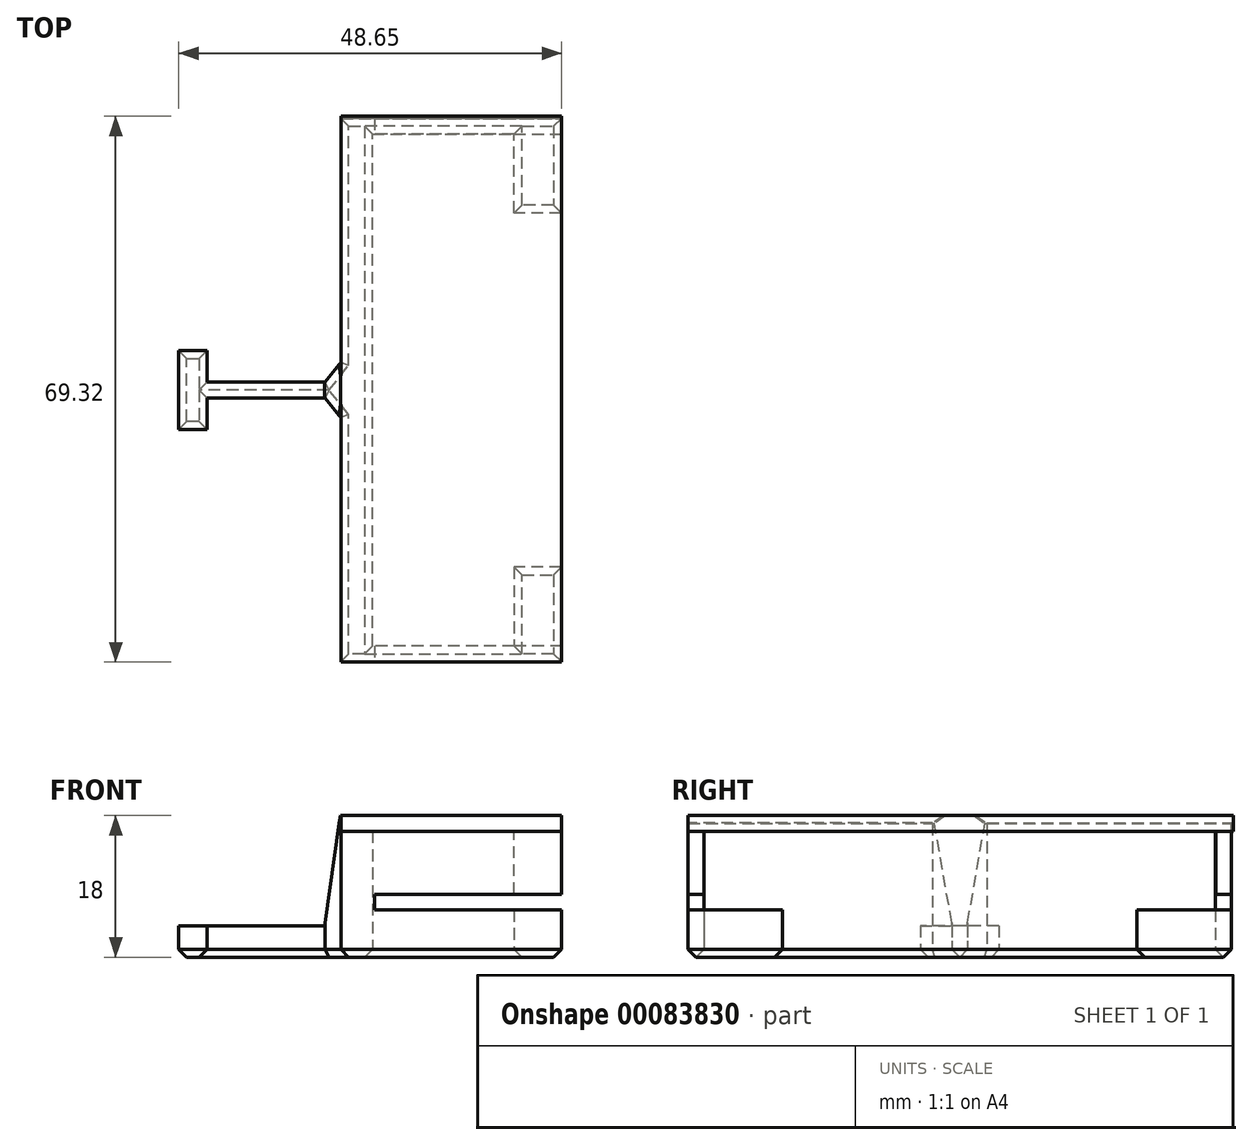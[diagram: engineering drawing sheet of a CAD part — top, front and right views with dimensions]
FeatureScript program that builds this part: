
annotation { "Feature Type Name" : "Feature", "Feature Type Description" : "" }
export const myFeature = defineFeature(function(context is Context, id is Id, definition is map)
    precondition{}
    {
        {
            var Q0;
            Q0=qCreatedBy(makeId("Top.planeOp"),FACE);
            var sketch = newSketch(context, id + "F0", { "sketchPlane" : qUnion([Q0])});
            skLineSegment(sketch, "E0", {"start": v(-12.1, 5) * mm, "end": v(-8.5, 5) * mm});
            skLineSegment(sketch, "E1", {"start": v(-8.5, 5) * mm, "end": v(-8.5, 1) * mm});
            skLineSegment(sketch, "E2", {"start": v(-8.5, 1) * mm, "end": v(6.5, 1) * mm});
            skLineSegment(sketch, "E3", {"start": v(6.5, 1) * mm, "end": v(8.5, 3.48) * mm});
            skLineSegment(sketch, "E4", {"start": v(8.5, 3.48) * mm, "end": v(8.5, 34.5) * mm});
            skLineSegment(sketch, "E5", {"start": v(8.5, 34.5) * mm, "end": v(36.5, 34.5) * mm});
            skLineSegment(sketch, "E6", {"start": v(36.5, 34.5) * mm, "end": v(36.5, 22.5) * mm});
            skLineSegment(sketch, "E7", {"start": v(36.5, 22.5) * mm, "end": v(30.5, 22.5) * mm});
            skLineSegment(sketch, "E8", {"start": v(30.5, 22.5) * mm, "end": v(30.5, 32.5) * mm});
            skLineSegment(sketch, "E9", {"start": v(30.5, 32.5) * mm, "end": v(12.5, 32.5) * mm});
            skLineSegment(sketch, "E10", {"start": v(12.5, 32.5) * mm, "end": v(12.5, 0) * mm});
            skLineSegment(sketch, "E11", {"start": v(-12.1, 5) * mm, "end": v(-12.1, 0) * mm});
            skLineSegment(sketch, "E12.MirrorCS", {"start": v(-12.1, -5) * mm, "end": v(-12.1, 0) * mm});
            skLineSegment(sketch, "E13.MirrorCS", {"start": v(-12.1, -5) * mm, "end": v(-8.5, -5) * mm});
            skLineSegment(sketch, "E14.MirrorCS", {"start": v(-8.5, -5) * mm, "end": v(-8.5, -1) * mm});
            skLineSegment(sketch, "E15.MirrorCS", {"start": v(-8.5, -1) * mm, "end": v(6.5, -1) * mm});
            skLineSegment(sketch, "E16.MirrorCS", {"start": v(6.5, -1) * mm, "end": v(8.5, -3.48) * mm});
            skLineSegment(sketch, "E17.MirrorCS", {"start": v(8.5, -3.48) * mm, "end": v(8.5, -34.5) * mm});
            skLineSegment(sketch, "E18.MirrorCS", {"start": v(8.5, -34.5) * mm, "end": v(36.5, -34.5) * mm});
            skLineSegment(sketch, "E19.MirrorCS", {"start": v(36.5, -34.5) * mm, "end": v(36.5, -22.5) * mm});
            skLineSegment(sketch, "E20.MirrorCS", {"start": v(36.5, -22.5) * mm, "end": v(30.5, -22.5) * mm});
            skLineSegment(sketch, "E21.MirrorCS", {"start": v(30.5, -22.5) * mm, "end": v(30.5, -32.5) * mm});
            skLineSegment(sketch, "E22.MirrorCS", {"start": v(30.5, -32.5) * mm, "end": v(12.5, -32.5) * mm});
            skLineSegment(sketch, "E23.MirrorCS", {"start": v(12.5, -32.5) * mm, "end": v(12.5, 0) * mm});
            skSolve(sketch);
        }
        {
            var Q0;
            Q0 = qSketchRegion(id + "F0", true);
            extrude(context, id + "F1", {"entities" : qUnion([Q0]), "depth" : 18 * mm});
        }
        {
            var Q0;
            Q0=makeQuery(id+"F1.opExtrude","CAP_FACE",FACE,{"disambiguationData":[OSD([sQuery(id+"F0.wireOp",EDGE,"E0"),sQuery(id+"F0.wireOp",EDGE,"E1"),sQuery(id+"F0.wireOp",EDGE,"E2"),sQuery(id+"F0.wireOp",EDGE,"E3"),sQuery(id+"F0.wireOp",EDGE,"E4"),sQuery(id+"F0.wireOp",EDGE,"E5"),sQuery(id+"F0.wireOp",EDGE,"E6"),sQuery(id+"F0.wireOp",EDGE,"E7"),sQuery(id+"F0.wireOp",EDGE,"E8"),sQuery(id+"F0.wireOp",EDGE,"E9"),sQuery(id+"F0.wireOp",EDGE,"E10"),sQuery(id+"F0.wireOp",EDGE,"E11"),sQuery(id+"F0.wireOp",EDGE,"E12.MirrorCS"),sQuery(id+"F0.wireOp",EDGE,"E13.MirrorCS"),sQuery(id+"F0.wireOp",EDGE,"E14.MirrorCS"),sQuery(id+"F0.wireOp",EDGE,"E15.MirrorCS"),sQuery(id+"F0.wireOp",EDGE,"E16.MirrorCS"),sQuery(id+"F0.wireOp",EDGE,"E17.MirrorCS"),sQuery(id+"F0.wireOp",EDGE,"E18.MirrorCS"),sQuery(id+"F0.wireOp",EDGE,"E19.MirrorCS"),sQuery(id+"F0.wireOp",EDGE,"E20.MirrorCS"),sQuery(id+"F0.wireOp",EDGE,"E21.MirrorCS"),sQuery(id+"F0.wireOp",EDGE,"E22.MirrorCS"),sQuery(id+"F0.wireOp",EDGE,"E23.MirrorCS")])],"isStart":false});
            var Q1;
            Q1=makeQuery(id+"F1.opExtrude","CAP_FACE",FACE,{"disambiguationData":[OSD([sQuery(id+"F0.wireOp",EDGE,"E0"),sQuery(id+"F0.wireOp",EDGE,"E1"),sQuery(id+"F0.wireOp",EDGE,"E2"),sQuery(id+"F0.wireOp",EDGE,"E3"),sQuery(id+"F0.wireOp",EDGE,"E4"),sQuery(id+"F0.wireOp",EDGE,"E5"),sQuery(id+"F0.wireOp",EDGE,"E6"),sQuery(id+"F0.wireOp",EDGE,"E7"),sQuery(id+"F0.wireOp",EDGE,"E8"),sQuery(id+"F0.wireOp",EDGE,"E9"),sQuery(id+"F0.wireOp",EDGE,"E10"),sQuery(id+"F0.wireOp",EDGE,"E11"),sQuery(id+"F0.wireOp",EDGE,"E12.MirrorCS"),sQuery(id+"F0.wireOp",EDGE,"E13.MirrorCS"),sQuery(id+"F0.wireOp",EDGE,"E14.MirrorCS"),sQuery(id+"F0.wireOp",EDGE,"E15.MirrorCS"),sQuery(id+"F0.wireOp",EDGE,"E16.MirrorCS"),sQuery(id+"F0.wireOp",EDGE,"E17.MirrorCS"),sQuery(id+"F0.wireOp",EDGE,"E18.MirrorCS"),sQuery(id+"F0.wireOp",EDGE,"E19.MirrorCS"),sQuery(id+"F0.wireOp",EDGE,"E20.MirrorCS"),sQuery(id+"F0.wireOp",EDGE,"E21.MirrorCS"),sQuery(id+"F0.wireOp",EDGE,"E22.MirrorCS"),sQuery(id+"F0.wireOp",EDGE,"E23.MirrorCS")])],"isStart":true});
            chamfer(context, id + "F2", {"entities" : qUnion([Q0, Q1]), "width" : 1 * mm, "tangentPropagation" : true});
        }
        {
            var Q0;
            Q0=qCreatedBy(makeId("Top.planeOp"),FACE);
            cPlane(context, id + "F3", {"entities" : qUnion([Q0]), "cplaneType" : CPlaneType.OFFSET, "offset" : 4 * mm, "width" : 150 * mm, "height" : 150 * mm});
        }
        {
            var Q0;
            Q0=qCreatedBy(id+"F3.planeOp",FACE);
            var sketch = newSketch(context, id + "F4", { "sketchPlane" : qUnion([Q0])});
            skLineSegment(sketch, "E24.bottom", {"start": v(-42.93, 8.18) * mm, "end": v(6.44, 8.18) * mm});
            skLineSegment(sketch, "E24.top", {"start": v(-42.93, -8.36) * mm, "end": v(6.44, -8.36) * mm});
            skLineSegment(sketch, "E24.left", {"start": v(-42.93, 8.18) * mm, "end": v(-42.93, -8.36) * mm});
            skLineSegment(sketch, "E24.right", {"start": v(6.44, 8.18) * mm, "end": v(6.44, -8.36) * mm});
            skSolve(sketch);
        }
        {
            var Q0;
            Q0=qCreatedBy(makeId("Top.planeOp"),FACE);
            cPlane(context, id + "F5", {"entities" : qUnion([Q0]), "cplaneType" : CPlaneType.OFFSET, "offset" : 18 * mm, "width" : 150 * mm, "height" : 150 * mm});
        }
        {
            var Q0;
            Q0=qCreatedBy(id+"F5.planeOp",FACE);
            var sketch = newSketch(context, id + "F6", { "sketchPlane" : qUnion([Q0])});
            skLineSegment(sketch, "E25.bottom", {"start": v(8.42, 7.41) * mm, "end": v(-16.63, 7.41) * mm});
            skLineSegment(sketch, "E25.top", {"start": v(8.42, -7.18) * mm, "end": v(-16.63, -7.18) * mm});
            skLineSegment(sketch, "E25.left", {"start": v(8.42, 7.41) * mm, "end": v(8.42, -7.18) * mm});
            skLineSegment(sketch, "E25.right", {"start": v(-16.63, 7.41) * mm, "end": v(-16.63, -7.18) * mm});
            skSolve(sketch);
        }
        {
            var Q1;
            Q1=makeQuery(id+"F4.imprint","IMPRINT",FACE,{"disambiguationData":[TD([[makeQuery(id+"F4.imprint","IMPRINT",EDGE,{"derivedFrom":sQuery(id+"F4.wireOp",EDGE,"E24.bottom")}),-1.0]])]});
            var Q2;
            Q2=makeQuery(id+"F6.imprint","IMPRINT",FACE,{"disambiguationData":[TD([[makeQuery(id+"F6.imprint","IMPRINT",EDGE,{"derivedFrom":sQuery(id+"F6.wireOp",EDGE,"E25.bottom")}),1.0]])]});
            loft(context, id + "F7", {"operationType" : NewBodyOperationType.REMOVE, "sheetProfilesArray" : [{ "sheetProfileEntities" : qUnion([Q1]) }, { "sheetProfileEntities" : qUnion([Q2]) }]});
        }
        {
            var Q0;
            Q0=qCreatedBy(id+"F5.planeOp",FACE);
            var sketch = newSketch(context, id + "F8", { "sketchPlane" : qUnion([Q0])});
            skLineSegment(sketch, "E26.bottom", {"start": v(8.52, 34.77) * mm, "end": v(36.55, 34.77) * mm});
            skLineSegment(sketch, "E26.top", {"start": v(8.52, -34.55) * mm, "end": v(36.55, -34.55) * mm});
            skLineSegment(sketch, "E26.left", {"start": v(8.52, 34.77) * mm, "end": v(8.52, -34.55) * mm});
            skLineSegment(sketch, "E26.right", {"start": v(36.55, 34.77) * mm, "end": v(36.55, -34.55) * mm});
            skSolve(sketch);
        }
        {
            var Q0;
            Q0 = qSketchRegion(id + "F8", true);
            extrude(context, id + "F9", {"entities" : qUnion([Q0]), "operationType" : NewBodyOperationType.ADD, "oppositeDirection" : true, "depth" : 2 * mm});
        }
        {
            var Q0;
            Q0=qCreatedBy(makeId("Top.planeOp"),FACE);
            cPlane(context, id + "F10", {"entities" : qUnion([Q0]), "cplaneType" : CPlaneType.OFFSET, "offset" : 6 * mm, "width" : 150 * mm, "height" : 150 * mm});
        }
        {
            var Q0;
            Q0=qCreatedBy(id+"F10.planeOp",FACE);
            var sketch = newSketch(context, id + "F11", { "sketchPlane" : qUnion([Q0])});
            skLineSegment(sketch, "E27.bottom", {"start": v(30.47, 32.52) * mm, "end": v(37.72, 32.52) * mm});
            skLineSegment(sketch, "E27.top", {"start": v(30.47, -32.48) * mm, "end": v(37.72, -32.48) * mm});
            skLineSegment(sketch, "E27.left", {"start": v(30.47, 32.52) * mm, "end": v(30.47, -32.48) * mm});
            skLineSegment(sketch, "E27.right", {"start": v(37.72, 32.52) * mm, "end": v(37.72, -32.48) * mm});
            skSolve(sketch);
        }
        {
            var Q0;
            Q0 = qSketchRegion(id + "F11", true);
            extrude(context, id + "F12", {"entities" : qUnion([Q0]), "operationType" : NewBodyOperationType.REMOVE, "depth" : 10 * mm});
        }
        {
            var Q0;
            Q0=qCreatedBy(id+"F10.planeOp",FACE);
            var sketch = newSketch(context, id + "F13", { "sketchPlane" : qUnion([Q0])});
            skLineSegment(sketch, "E28.bottom", {"start": v(12.76, 37.5) * mm, "end": v(50.5, 37.5) * mm});
            skLineSegment(sketch, "E28.top", {"start": v(12.76, -37.88) * mm, "end": v(50.5, -37.88) * mm});
            skLineSegment(sketch, "E28.left", {"start": v(12.76, 37.5) * mm, "end": v(12.76, -37.88) * mm});
            skLineSegment(sketch, "E28.right", {"start": v(50.5, 37.5) * mm, "end": v(50.5, -37.88) * mm});
            skSolve(sketch);
        }
        {
            var Q0;
            Q0 = qSketchRegion(id + "F13", true);
            extrude(context, id + "F14", {"entities" : qUnion([Q0]), "operationType" : NewBodyOperationType.REMOVE, "depth" : 2 * mm});
        }
    });
